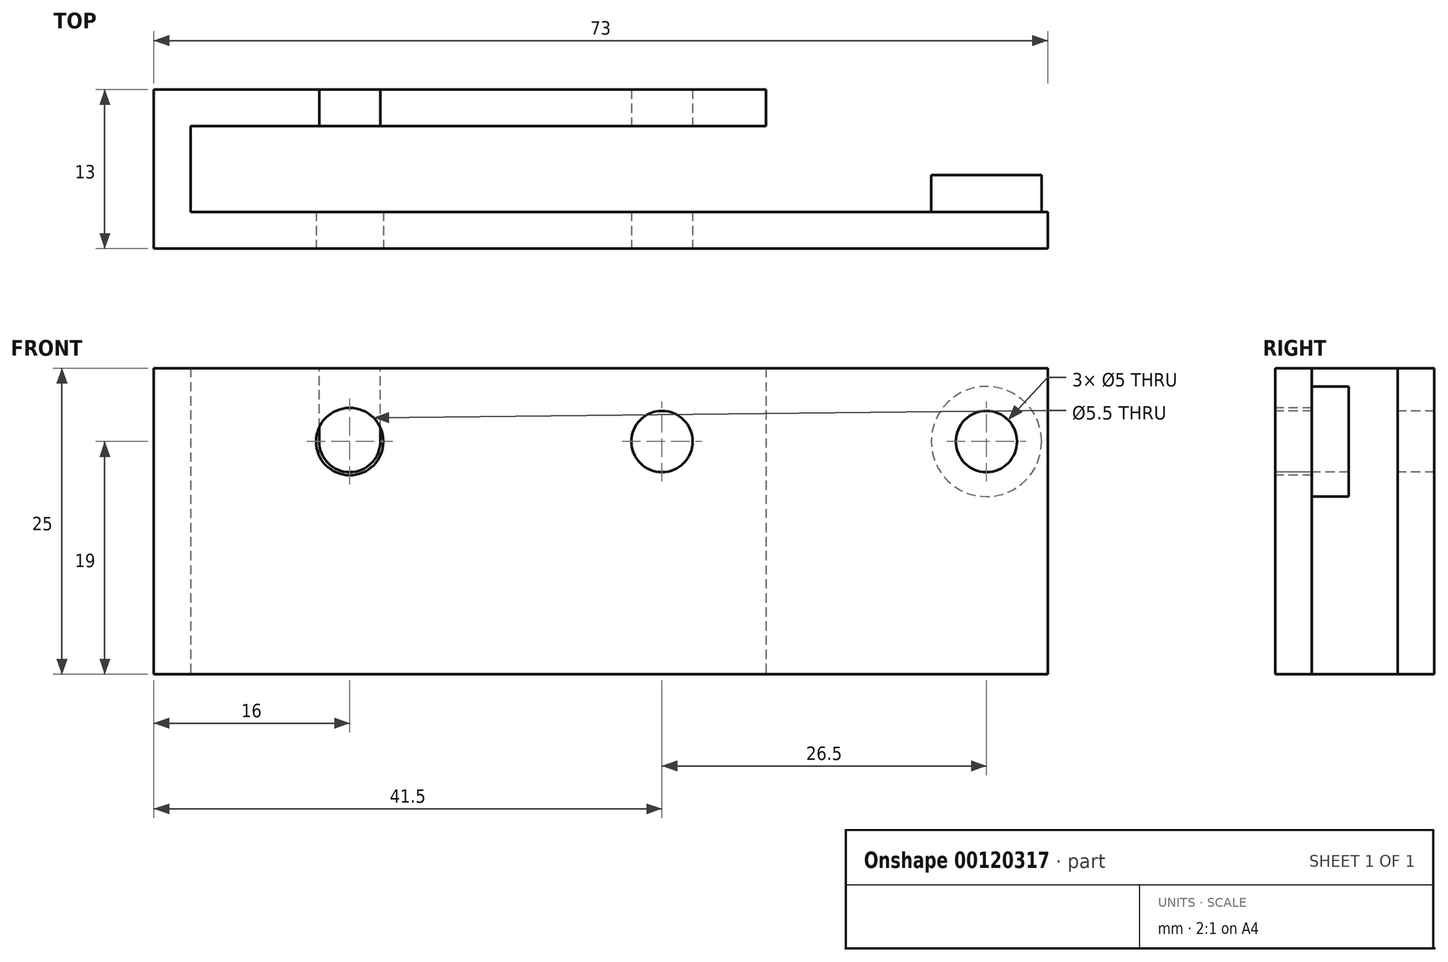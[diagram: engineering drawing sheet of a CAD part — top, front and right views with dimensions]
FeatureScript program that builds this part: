
annotation { "Feature Type Name" : "Feature", "Feature Type Description" : "" }
export const myFeature = defineFeature(function(context is Context, id is Id, definition is map)
    precondition{}
    {
        {
            var Q0;
            Q0=qCreatedBy(makeId("Front.planeOp"),FACE);
            var sketch = newSketch(context, id + "F0", { "sketchPlane" : qUnion([Q0])});
            skLineSegment(sketch, "E0.bottom", {"start": v(-24, 12.5) * mm, "end": v(24, 12.5) * mm});
            skLineSegment(sketch, "E0.top", {"start": v(-24, -12.5) * mm, "end": v(24, -12.5) * mm});
            skLineSegment(sketch, "E0.left", {"start": v(-24, 12.5) * mm, "end": v(-24, -12.5) * mm});
            skLineSegment(sketch, "E0.right", {"start": v(24, 12.5) * mm, "end": v(24, -12.5) * mm});
            skPoint(sketch, "E0.middle", {"position": v(0, 0) * mm});
            skSolve(sketch);
        }
        {
            var Q0;
            Q0 = qSketchRegion(id + "F0", true);
            extrude(context, id + "F1", {"entities" : qUnion([Q0]), "depth" : 3 * mm});
        }
        {
            var Q0;
            Q0=qCreatedBy(makeId("Front.planeOp"),FACE);
            var sketch = newSketch(context, id + "F2", { "sketchPlane" : qUnion([Q0])});
            skLineSegment(sketch, "E1.bottom", {"start": v(-27, 12.5) * mm, "end": v(-24, 12.5) * mm});
            skLineSegment(sketch, "E1.top", {"start": v(-27, -12.5) * mm, "end": v(-24, -12.5) * mm});
            skLineSegment(sketch, "E1.left", {"start": v(-27, 12.5) * mm, "end": v(-27, -12.5) * mm});
            skLineSegment(sketch, "E1.right", {"start": v(-24, 12.5) * mm, "end": v(-24, -12.5) * mm});
            skSolve(sketch);
        }
        {
            var Q0;
            Q0 = qSketchRegion(id + "F2", true);
            extrude(context, id + "F3", {"entities" : qUnion([Q0]), "operationType" : NewBodyOperationType.ADD, "depth" : 13 * mm});
        }
        {
            var Q0;
            Q0=makeQuery(id+"F1.opExtrude","CAP_FACE",FACE,{"disambiguationData":[OSD([sQuery(id+"F0.wireOp",EDGE,"E0.bottom"),sQuery(id+"F0.wireOp",EDGE,"E0.top"),sQuery(id+"F0.wireOp",EDGE,"E0.left"),sQuery(id+"F0.wireOp",EDGE,"E0.right")])],"isStart":false});
            var sketch = newSketch(context, id + "F4", { "sketchPlane" : qUnion([Q0])});
            skCircle(sketch, "E2", {"center": v(-11, 6.5) * mm, "radius": 12.5 * mm, "construction": true});
            skCircle(sketch, "E3", {"center": v(14.5, 6.5) * mm, "radius": 15 * mm, "construction": true});
            skCircle(sketch, "E4", {"center": v(14.5, 6.5) * mm, "radius": 10 * mm, "construction": true});
            skCircle(sketch, "E5", {"center": v(-11, 6.5) * mm, "radius": 10 * mm, "construction": true});
            skCircle(sketch, "E6", {"center": v(14.5, 6.5) * mm, "radius": 12.5 * mm, "construction": true});
            skCircle(sketch, "E7", {"center": v(14.5, 6.5) * mm, "radius": 17.5 * mm, "construction": true});
            skCircle(sketch, "E8", {"center": v(-11, 6.5) * mm, "radius": 6.88 * mm, "construction": true});
            skCircle(sketch, "E9", {"center": v(-11, 6.5) * mm, "radius": 2.5 * mm});
            skCircle(sketch, "E10", {"center": v(14.5, 6.5) * mm, "radius": 2.5 * mm});
            skCircle(sketch, "E11", {"center": v(39.5, 6.5) * mm, "radius": 15 * mm, "construction": true});
            skCircle(sketch, "E12", {"center": v(39.5, 6.5) * mm, "radius": 17.5 * mm, "construction": true});
            skSolve(sketch);
        }
        {
            var Q0;
            Q0 = qSketchRegion(id + "F4", true);
            extrude(context, id + "F5", {"entities" : qUnion([Q0]), "operationType" : NewBodyOperationType.REMOVE, "oppositeDirection" : true, "depth" : 3 * mm});
        }
        {
            var Q0;
            Q0=makeQuery(id+"F4.imprint","IMPRINT",FACE,{"disambiguationData":[TD([[makeQuery(id+"F4.imprint","IMPRINT",EDGE,{"derivedFrom":sQuery(id+"F4.wireOp",EDGE,"E9")}),-1.0]])]});
            var sketch = newSketch(context, id + "F6", { "sketchPlane" : qUnion([Q0])});
            skLineSegment(sketch, "E13.bottom", {"start": v(23, 12.5) * mm, "end": v(24, 12.5) * mm});
            skLineSegment(sketch, "E13.top", {"start": v(23, -12.5) * mm, "end": v(24, -12.5) * mm});
            skLineSegment(sketch, "E13.left", {"start": v(23, 12.5) * mm, "end": v(23, -12.5) * mm});
            skLineSegment(sketch, "E13.right", {"start": v(24, 12.5) * mm, "end": v(24, -12.5) * mm});
            skSolve(sketch);
        }
        {
            var Q0;
            Q0 = qSketchRegion(id + "F6", true);
            extrude(context, id + "F7", {"entities" : qUnion([Q0]), "operationType" : NewBodyOperationType.REMOVE, "oppositeDirection" : true, "depth" : 3 * mm});
        }
        {
            var Q0;
            Q0=makeQuery(id+"F3.opExtrude","SWEPT_FACE",FACE,{"disambiguationData":[OSD([sQuery(id+"F2.wireOp",EDGE,"E1.right")])]});
            var sketch = newSketch(context, id + "F8", { "sketchPlane" : qUnion([Q0])});
            skLineSegment(sketch, "E14.bottom", {"start": v(-13, 12.5) * mm, "end": v(-10, 12.5) * mm});
            skLineSegment(sketch, "E14.top", {"start": v(-13, -12.5) * mm, "end": v(-10, -12.5) * mm});
            skLineSegment(sketch, "E14.left", {"start": v(-13, 12.5) * mm, "end": v(-13, -12.5) * mm});
            skLineSegment(sketch, "E14.right", {"start": v(-10, 12.5) * mm, "end": v(-10, -12.5) * mm});
            skSolve(sketch);
        }
        {
            var Q0;
            Q0 = qSketchRegion(id + "F8", true);
            extrude(context, id + "F9", {"entities" : qUnion([Q0]), "operationType" : NewBodyOperationType.ADD, "depth" : 70 * mm});
        }
        {
            var Q0;
            Q0=makeQuery(id+"F9.boolean.opBoolean","MERGE",FACE,{"derivedFrom":[makeQuery(id+"F3.opExtrude","CAP_FACE",FACE,{"disambiguationData":[OSD([sQuery(id+"F2.wireOp",EDGE,"E1.bottom"),sQuery(id+"F2.wireOp",EDGE,"E1.top"),sQuery(id+"F2.wireOp",EDGE,"E1.left"),sQuery(id+"F2.wireOp",EDGE,"E1.right")])],"isStart":false}),makeQuery(id+"F9.opExtrude","SWEPT_FACE",FACE,{"disambiguationData":[OSD([sQuery(id+"F8.wireOp",EDGE,"E14.left")])]})]});
            var sketch = newSketch(context, id + "F10", { "sketchPlane" : qUnion([Q0])});
            skCircle(sketch, "E15", {"center": v(-11, 6.5) * mm, "radius": 2.75 * mm});
            skCircle(sketch, "E16", {"center": v(14.5, 6.5) * mm, "radius": 2.5 * mm});
            skCircle(sketch, "E17", {"center": v(41, 6.5) * mm, "radius": 2.5 * mm});
            skSolve(sketch);
        }
        {
            var Q0;
            Q0 = qSketchRegion(id + "F10", true);
            extrude(context, id + "F11", {"entities" : qUnion([Q0]), "operationType" : NewBodyOperationType.REMOVE, "oppositeDirection" : true, "depth" : 3 * mm});
        }
        {
            var Q0;
            Q0=makeQuery(id+"F9.opExtrude","SWEPT_FACE",FACE,{"disambiguationData":[OSD([sQuery(id+"F8.wireOp",EDGE,"E14.right")])]});
            var sketch = newSketch(context, id + "F12", { "sketchPlane" : qUnion([Q0])});
            skCircle(sketch, "E18", {"center": v(-41, 6.5) * mm, "radius": 4.5 * mm});
            skCircle(sketch, "E19", {"center": v(-41, 6.5) * mm, "radius": 2.5 * mm});
            skSolve(sketch);
        }
        {
            var Q0;
            Q0 = qSketchRegion(id + "F12", true);
            extrude(context, id + "F13", {"entities" : qUnion([Q0]), "operationType" : NewBodyOperationType.ADD, "depth" : 3 * mm});
        }
        {
            var Q0;
            Q0=qCreatedBy(makeId("Front.planeOp"),FACE);
            var sketch = newSketch(context, id + "F14", { "sketchPlane" : qUnion([Q0])});
            skLineSegment(sketch, "E20", {"start": v(-8.5, 6.5) * mm, "end": v(-13.5, 6.5) * mm, "construction": true});
            skLineSegment(sketch, "E21", {"start": v(-8.5, 6.5) * mm, "end": v(-8.5, 12.5) * mm});
            skLineSegment(sketch, "E22", {"start": v(-13.5, 6.5) * mm, "end": v(-13.5, 12.5) * mm});
            skLineSegment(sketch, "E23", {"start": v(-13.5, 12.5) * mm, "end": v(-8.5, 12.5) * mm});
            skArc(sketch, "E24", {"start": v(-8.5, 6.5) * mm, "mid": v(-11, 9) * mm, "end": v(-13.5, 6.5) * mm});
            skSolve(sketch);
        }
        {
            var Q0;
            Q0 = qSketchRegion(id + "F14", true);
            extrude(context, id + "F15", {"entities" : qUnion([Q0]), "operationType" : NewBodyOperationType.REMOVE, "depth" : 3 * mm});
        }
    });
